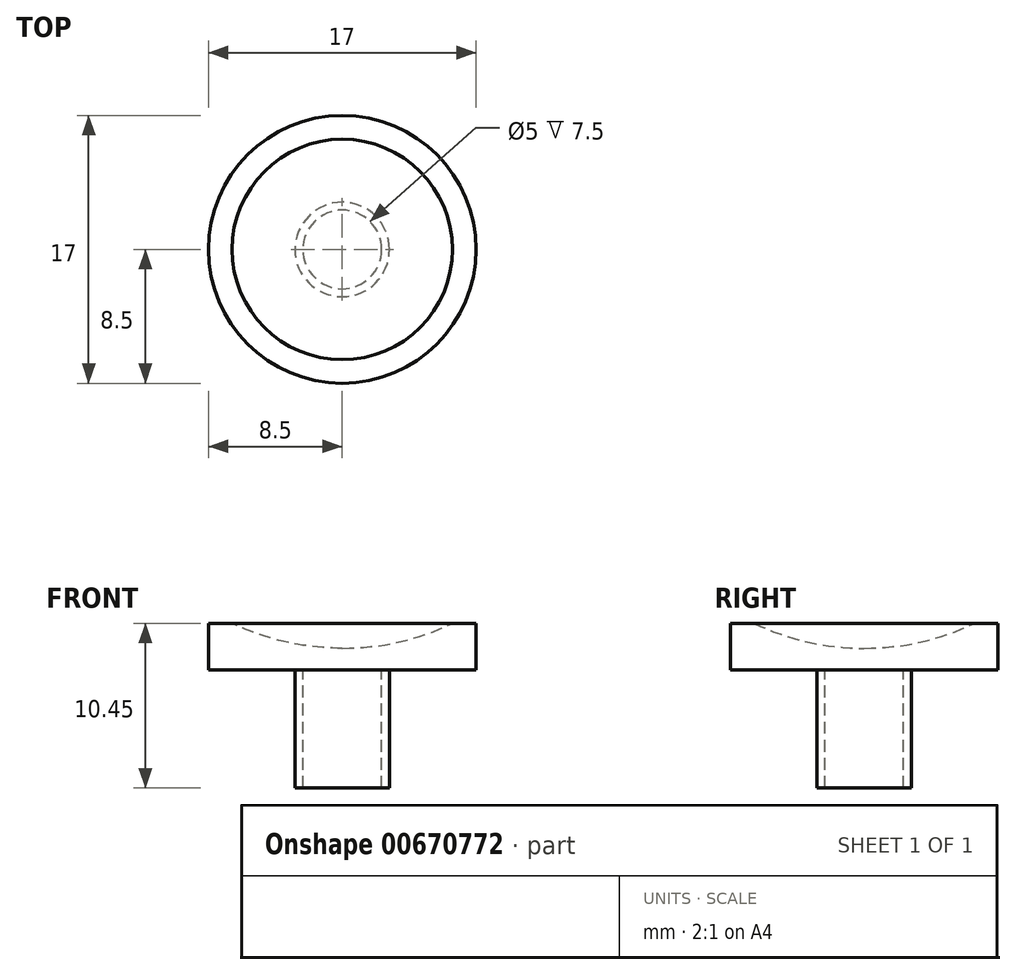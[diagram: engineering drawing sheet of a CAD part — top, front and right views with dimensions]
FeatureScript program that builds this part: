
annotation { "Feature Type Name" : "Feature", "Feature Type Description" : "" }
export const myFeature = defineFeature(function(context is Context, id is Id, definition is map)
    precondition{}
    {
        {
            var Q0;
            Q0=qCreatedBy(makeId("Front.planeOp"),FACE);
            var sketch = newSketch(context, id + "F0", { "sketchPlane" : qUnion([Q0])});
            skLineSegment(sketch, "E0", {"start": v(-3, 0) * mm, "end": v(-3, 7.5) * mm});
            skLineSegment(sketch, "E1", {"start": v(-3, 7.5) * mm, "end": v(-8.5, 7.5) * mm});
            skLineSegment(sketch, "E2", {"start": v(-8.5, 7.5) * mm, "end": v(-8.5, 10.45) * mm});
            skLineSegment(sketch, "E3", {"start": v(-8.5, 10.45) * mm, "end": v(-7, 10.45) * mm});
            skLineSegment(sketch, "E4", {"start": v(-3, 0) * mm, "end": v(-2.5, 0) * mm});
            skLineSegment(sketch, "E5", {"start": v(-2.5, 0) * mm, "end": v(-2.5, 7.5) * mm});
            skLineSegment(sketch, "E6", {"start": v(-2.5, 7.5) * mm, "end": v(0, 7.5) * mm});
            skLineSegment(sketch, "E7", {"start": v(0, 8.87) * mm, "end": v(0, 7.5) * mm});
            skArc(sketch, "E8", {"start": v(-7, 10.45) * mm, "mid": v(-3.59, 9.27) * mm, "end": v(0, 8.87) * mm});
            skPoint(sketch, "E9.orphan", {"position": v(0, 13.04) * mm});
            skSolve(sketch);
        }
        {
            var Q0;
            Q0 = qSketchRegion(id + "F0", true);
            var Q1;
            Q1=sQuery(id+"F0.wireOp",EDGE,"E7");
            revolve(context, id + "F1", {"entities" : qUnion([Q0]), "axis" : qUnion([Q1]), "revolveType" : RevolveType.FULL});
        }
    });
